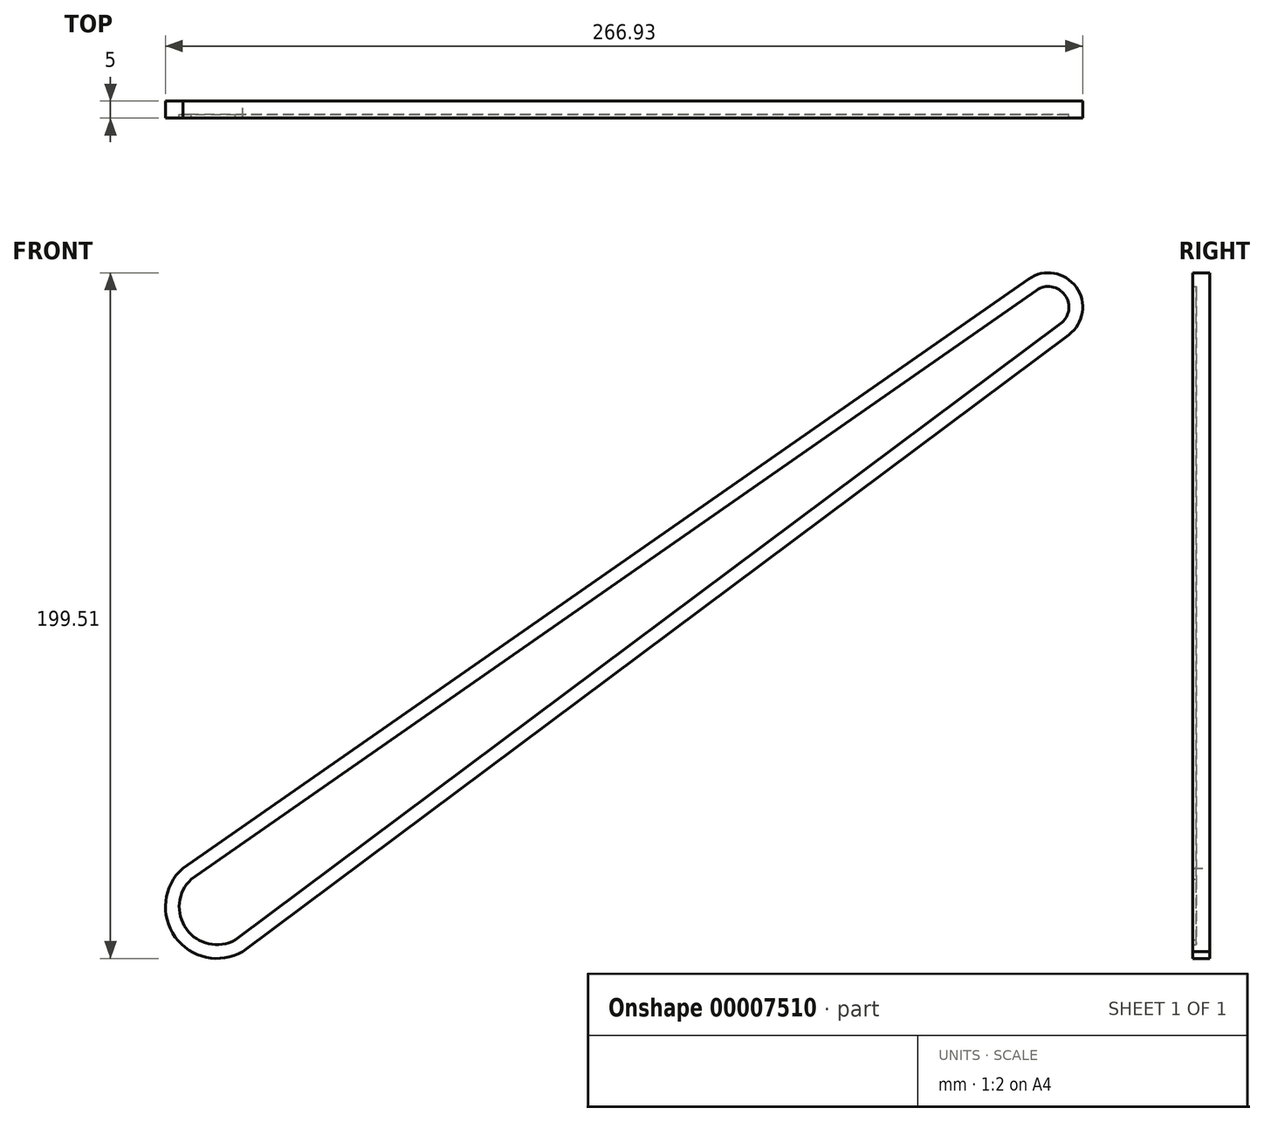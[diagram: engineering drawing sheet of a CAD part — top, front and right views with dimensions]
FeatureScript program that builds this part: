
annotation { "Feature Type Name" : "Feature", "Feature Type Description" : "" }
export const myFeature = defineFeature(function(context is Context, id is Id, definition is map)
    precondition{}
    {
        {
            var Q0;
            Q0=qCreatedBy(makeId("Front.planeOp"),FACE);
            var sketch = newSketch(context, id + "F0", { "sketchPlane" : qUnion([Q0])});
            skCircle(sketch, "E0", {"center": v(0, 0) * mm, "radius": 15 * mm});
            skCircle(sketch, "E1", {"center": v(241.93, 174.5) * mm, "radius": 10 * mm});
            skLineSegment(sketch, "E2", {"start": v(236.21, 182.71) * mm, "end": v(-9.95, 11.23) * mm});
            skLineSegment(sketch, "E3", {"start": v(7.52, -12.98) * mm, "end": v(247.91, 166.5) * mm});
            skLineSegment(sketch, "E4", {"start": v(241.93, 174.5) * mm, "end": v(0, 0) * mm});
            skSolve(sketch);
        }
        {
            var Q0;
            {var subQ0=sQuery(id+"F0.wireOp",EDGE,"E2");var subQ1=sQuery(id+"F0.wireOp",EDGE,"E0");var subQ3=makeQuery(id+"F0.imprint","INTERSECT",VERTEX,{"disambiguationData":[OD(0.0)],"derivedFrom":[subQ1,subQ0]});Q0=makeQuery(id+"F0.imprint","IMPRINT",FACE,{"disambiguationData":[TD([[makeQuery(id+"F0.imprint","IMPRINT",EDGE,{"disambiguationData":[TD([[subQ3,-1.0]])],"derivedFrom":subQ1}),1.0]])]});}
            var Q1;
            {var subQ0=sQuery(id+"F0.wireOp",EDGE,"E3");Q1=makeQuery(id+"F0.imprint","IMPRINT",FACE,{"disambiguationData":[TD([[makeQuery(id+"F0.imprint","IMPRINT",EDGE,{"derivedFrom":subQ0}),1.0]])]});}
            var Q2;
            {var subQ0=sQuery(id+"F0.wireOp",EDGE,"E1");var subQ2=makeQuery(id+"F0.imprint","INTERSECT",VERTEX,{"derivedFrom":[subQ0,sQuery(id+"F0.wireOp",EDGE,"E2")]});Q2=makeQuery(id+"F0.imprint","IMPRINT",FACE,{"disambiguationData":[TD([[makeQuery(id+"F0.imprint","IMPRINT",EDGE,{"disambiguationData":[TD([[subQ2,-1.0]])],"derivedFrom":subQ0}),1.0]])]});}
            var Q3;
            {var subQ3=sQuery(id+"F0.wireOp",EDGE,"E0");var subQ5=sQuery(id+"F0.wireOp",EDGE,"E2");var subQ6=makeQuery(id+"F0.imprint","INTERSECT",VERTEX,{"disambiguationData":[OD(1.0)],"derivedFrom":[subQ3,subQ5]});Q3=makeQuery(id+"F0.imprint","IMPRINT",FACE,{"disambiguationData":[TD([[makeQuery(id+"F0.imprint","IMPRINT",EDGE,{"disambiguationData":[TD([[subQ6,1.0]])],"derivedFrom":subQ3}),-1.0]])]});}
            extrude(context, id + "F1", {"entities" : qUnion([Q0, Q1, Q2, Q3]), "depth" : 5 * mm});
        }
        {
            var Q0;
            Q0=makeQuery(id+"F1.opExtrude","CAP_FACE",FACE,{"disambiguationData":[OSD([sQuery(id+"F0.wireOp",EDGE,"E0"),sQuery(id+"F0.wireOp",EDGE,"E1"),sQuery(id+"F0.wireOp",EDGE,"E2"),sQuery(id+"F0.wireOp",EDGE,"E3")])],"isStart":false});
            shell(context, id + "F2", {"entities" : qUnion([Q0]), "thickness" : 4 * mm});
        }
    });
